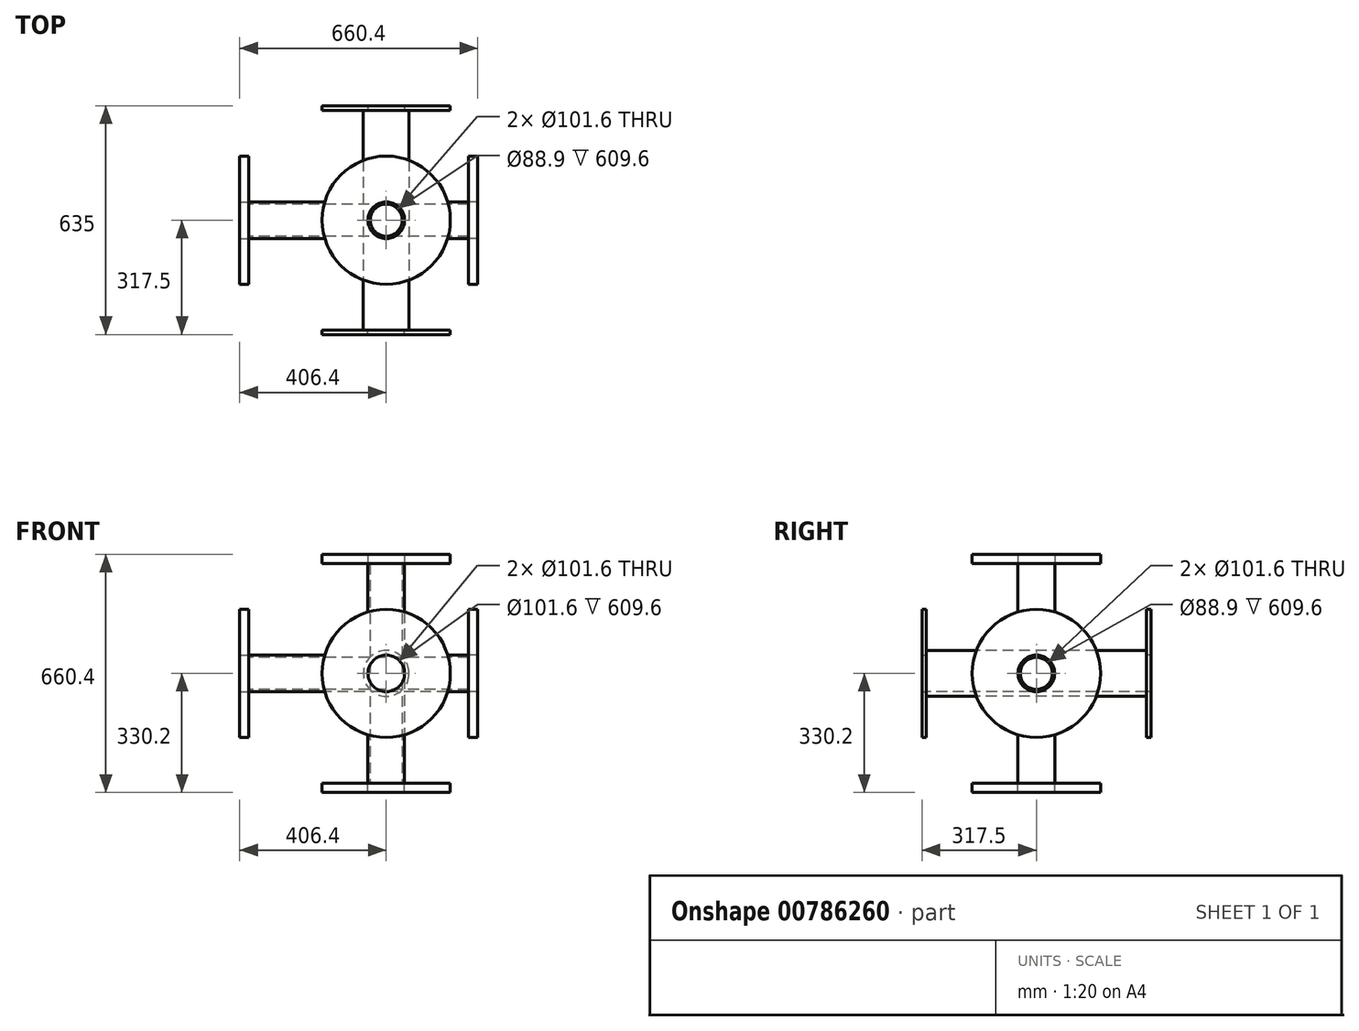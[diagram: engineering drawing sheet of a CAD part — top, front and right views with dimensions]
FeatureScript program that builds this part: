
annotation { "Feature Type Name" : "Feature", "Feature Type Description" : "" }
export const myFeature = defineFeature(function(context is Context, id is Id, definition is map)
    precondition{}
    {
        {
            var Q0;
            Q0=qCreatedBy(makeId("Top.planeOp"),FACE);
            var sketch = newSketch(context, id + "F0", { "sketchPlane" : qUnion([Q0])});
            skCircle(sketch, "E0", {"center": v(0, 0) * mm, "radius": 50.8 * mm});
            skCircle(sketch, "E1", {"center": v(0, 0) * mm, "radius": 44.45 * mm});
            skSolve(sketch);
        }
        {
            var Q0;
            Q0=makeQuery(id+"F0.imprint","IMPRINT",FACE,{"disambiguationData":[TD([[makeQuery(id+"F0.imprint","IMPRINT",EDGE,{"derivedFrom":sQuery(id+"F0.wireOp",EDGE,"E0")}),1.0]])]});
            extrude(context, id + "F1", {"entities" : qUnion([Q0]), "endBound" : BoundingType.SYMMETRIC, "depth" : 609.6 * mm, "offsetDistance" : 25.4 * mm});
        }
        {
            var Q0;
            Q0=makeQuery(id+"F1.opExtrude","CAP_FACE",FACE,{"disambiguationData":[OSD([sQuery(id+"F0.wireOp",EDGE,"E0"),sQuery(id+"F0.wireOp",EDGE,"E1")])],"isStart":false});
            var sketch = newSketch(context, id + "F2", { "sketchPlane" : qUnion([Q0])});
            skPoint(sketch, "E2", {"position": v(0, 0) * mm});
            skLineSegment(sketch, "E3", {"start": v(0, -50.8) * mm, "end": v(0, 50.8) * mm, "construction": true});
            skCircle(sketch, "E4", {"center": v(0, 0) * mm, "radius": 177.8 * mm});
            skCircle(sketch, "E5", {"center": v(0, 0) * mm, "radius": 50.8 * mm});
            skSolve(sketch);
        }
        {
            var Q0;
            Q0 = qSketchRegion(id + "F2", true);
            var Q1;
            Q1 = qSketchRegion(id + "F4", true);
            extrude(context, id + "F3", {"entities" : qUnion([Q0, Q1]), "depth" : 25.4 * mm, "offsetDistance" : 25.4 * mm});
        }
        {
            var Q0;
            Q0=makeQuery(id+"F1.opExtrude","CAP_FACE",FACE,{"disambiguationData":[OSD([sQuery(id+"F0.wireOp",EDGE,"E0"),sQuery(id+"F0.wireOp",EDGE,"E1")])],"isStart":true});
            var sketch = newSketch(context, id + "F4", { "sketchPlane" : qUnion([Q0])});
            skPoint(sketch, "E6", {"position": v(0, 0) * mm});
            skCircle(sketch, "E7", {"center": v(0, 0) * mm, "radius": 177.8 * mm});
            skSolve(sketch);
        }
        {
            var Q0;
            Q0=qCreatedBy(makeId("Right.planeOp"),FACE);
            var sketch = newSketch(context, id + "F5", { "sketchPlane" : qUnion([Q0])});
            skCircle(sketch, "E8", {"center": v(0, 0) * mm, "radius": 63.5 * mm});
            skCircle(sketch, "E9", {"center": v(0, 0) * mm, "radius": 50.8 * mm});
            skSolve(sketch);
        }
        {
            var Q0;
            Q0 = qSketchRegion(id + "F5", true);
            extrude(context, id + "F6", {"entities" : qUnion([Q0]), "endBound" : BoundingType.SYMMETRIC, "depth" : 609.6 * mm, "offsetDistance" : 25.4 * mm});
        }
        {
            var Q0;
            Q0=makeQuery(id+"F6.opExtrude","CAP_FACE",FACE,{"disambiguationData":[OSD([sQuery(id+"F5.wireOp",EDGE,"E8"),sQuery(id+"F5.wireOp",EDGE,"E9")])],"isStart":false});
            var sketch = newSketch(context, id + "F7", { "sketchPlane" : qUnion([Q0])});
            skPoint(sketch, "E10", {"position": v(0, 0) * mm});
            skCircle(sketch, "E11", {"center": v(0, 0) * mm, "radius": 177.8 * mm});
            skCircle(sketch, "E12", {"center": v(0, 0) * mm, "radius": 50.8 * mm});
            skSolve(sketch);
        }
        {
            var Q0;
            Q0 = qSketchRegion(id + "F7", true);
            extrude(context, id + "F8", {"entities" : qUnion([Q0]), "depth" : 12.7 * mm, "offsetDistance" : 25.4 * mm});
        }
        {
            var Q0;
            Q0=makeQuery(id+"F8.opExtrude","SWEPT_BODY",BODY,{"disambiguationData":[OSD([sQuery(id+"F7.wireOp",EDGE,"E11"),sQuery(id+"F7.wireOp",EDGE,"E12")])]});
            var Q1;
            Q1=qCreatedBy(makeId("Right.planeOp"),FACE);
            mirror(context, id + "F9", {"entities" : qUnion([Q0]), "mirrorPlane" : qUnion([Q1])});
        }
        {
            var Q0;
            Q0=makeQuery(id+"Fdzxom4iDK7pz1L_1.opExtrude","SWEPT_BODY",BODY,{"disambiguationData":[OSD([sQuery(id+"F4.wireOp",EDGE,"E7")])]});
            var Q1;
            Q1=makeQuery(id+"F1.opExtrude","SWEPT_BODY",BODY,{"disambiguationData":[OSD([sQuery(id+"F0.wireOp",EDGE,"E0"),sQuery(id+"F0.wireOp",EDGE,"E1")])]});
            var Q2;
            Q2=makeQuery(id+"F3.opExtrude","SWEPT_BODY",BODY,{"disambiguationData":[OSD([sQuery(id+"F2.wireOp",EDGE,"E4")])]});
            var Q3;
            Q3=makeQuery(id+"F9.opPattern","COPY",EDGE,{"derivedFrom":makeQuery(id+"F8.opExtrude","CAP_EDGE",EDGE,{"disambiguationData":[OSD([sQuery(id+"F7.wireOp",EDGE,"E11")])],"isStart":false}),"instanceName":"1"});
            transform(context, id + "F10", {"entities" : qUnion([Q0, Q1, Q2]), "transformType" : TransformType.ROTATION, "transformAxis" : qUnion([Q3]), "angle" : 90 * degree, "makeCopy" : false});
        }
        {
            var Q0;
            Q0=makeQuery(id+"Fdzxom4iDK7pz1L_1.opExtrude","SWEPT_BODY",BODY,{"disambiguationData":[OSD([sQuery(id+"F4.wireOp",EDGE,"E7")])]});
            var Q1;
            Q1=makeQuery(id+"F1.opExtrude","SWEPT_BODY",BODY,{"disambiguationData":[OSD([sQuery(id+"F0.wireOp",EDGE,"E0"),sQuery(id+"F0.wireOp",EDGE,"E1")])]});
            var Q2;
            Q2=makeQuery(id+"F3.opExtrude","SWEPT_BODY",BODY,{"disambiguationData":[OSD([sQuery(id+"F2.wireOp",EDGE,"E4")])]});
            var Q3;
            Q3=makeQuery(id+"F6.opExtrude","SWEPT_FACE",FACE,{"disambiguationData":[OSD([sQuery(id+"F5.wireOp",EDGE,"E8")])]});
            transform(context, id + "F11", {"entities" : qUnion([Q0, Q1, Q2]), "transformType" : TransformType.ROTATION, "transformAxis" : qUnion([Q3]), "angle" : 90 * degree, "makeCopy" : false});
        }
        {
            var Q0;
            Q0=makeQuery(id+"F3.opExtrude","SWEPT_BODY",BODY,{"disambiguationData":[OSD([sQuery(id+"F2.wireOp",EDGE,"E4"),sQuery(id+"F2.wireOp",EDGE,"E5")])]});
            var Q1;
            Q1=qCreatedBy(makeId("Top.planeOp"),FACE);
            mirror(context, id + "F12", {"entities" : qUnion([Q0]), "mirrorPlane" : qUnion([Q1])});
        }
        {
            var Q0;
            Q0=makeQuery(id+"F6.opExtrude","SWEPT_BODY",BODY,{"disambiguationData":[OSD([sQuery(id+"F5.wireOp",EDGE,"E8"),sQuery(id+"F5.wireOp",EDGE,"E9")])]});
            var Q1;
            Q1=makeQuery(id+"F9.opPattern","COPY",BODY,{"derivedFrom":makeQuery(id+"F8.opExtrude","SWEPT_BODY",BODY,{"disambiguationData":[OSD([sQuery(id+"F7.wireOp",EDGE,"E11"),sQuery(id+"F7.wireOp",EDGE,"E12")])]}),"instanceName":"1"});
            var Q2;
            Q2=makeQuery(id+"F8.opExtrude","SWEPT_BODY",BODY,{"disambiguationData":[OSD([sQuery(id+"F7.wireOp",EDGE,"E11"),sQuery(id+"F7.wireOp",EDGE,"E12")])]});
            var Q3;
            Q3=makeQuery(id+"F3.opExtrude","CAP_EDGE",EDGE,{"disambiguationData":[OSD([sQuery(id+"F2.wireOp",EDGE,"E4")])],"isStart":false});
            transform(context, id + "F13", {"entities" : qUnion([Q0, Q1, Q2]), "transformType" : TransformType.ROTATION, "transformAxis" : qUnion([Q3]), "angle" : 90 * degree, "makeCopy" : false});
        }
        {
            var Q0;
            Q0=makeQuery(id+"F1.opExtrude","SWEPT_BODY",BODY,{"disambiguationData":[OSD([sQuery(id+"F0.wireOp",EDGE,"E0"),sQuery(id+"F0.wireOp",EDGE,"E1")])]});
            var Q1;
            Q1=makeQuery(id+"F3.opExtrude","SWEPT_BODY",BODY,{"disambiguationData":[OSD([sQuery(id+"F2.wireOp",EDGE,"E4"),sQuery(id+"F2.wireOp",EDGE,"E5")])]});
            var Q2;
            Q2=makeQuery(id+"F12.opPattern","COPY",BODY,{"derivedFrom":makeQuery(id+"F3.opExtrude","SWEPT_BODY",BODY,{"disambiguationData":[OSD([sQuery(id+"F2.wireOp",EDGE,"E4"),sQuery(id+"F2.wireOp",EDGE,"E5")])]}),"instanceName":"1"});
            var Q3;
            Q3=makeQuery(id+"F8.opExtrude","CAP_EDGE",EDGE,{"disambiguationData":[OSD([sQuery(id+"F7.wireOp",EDGE,"E11")])],"isStart":false});
            transform(context, id + "F14", {"entities" : qUnion([Q0, Q1, Q2]), "transformType" : TransformType.ROTATION, "transformAxis" : qUnion([Q3]), "angle" : 90 * degree, "makeCopy" : true});
        }
        {
            var Q0;
            Q0=makeQuery(id+"F14.opPattern","COPY",BODY,{"derivedFrom":makeQuery(id+"F1.opExtrude","SWEPT_BODY",BODY,{"disambiguationData":[OSD([sQuery(id+"F0.wireOp",EDGE,"E0"),sQuery(id+"F0.wireOp",EDGE,"E1")])]}),"instanceName":"1"});
            var Q1;
            Q1=makeQuery(id+"F14.opPattern","COPY",BODY,{"derivedFrom":makeQuery(id+"F12.opPattern","COPY",BODY,{"derivedFrom":makeQuery(id+"F3.opExtrude","SWEPT_BODY",BODY,{"disambiguationData":[OSD([sQuery(id+"F2.wireOp",EDGE,"E4"),sQuery(id+"F2.wireOp",EDGE,"E5")])]}),"instanceName":"1"}),"instanceName":"1"});
            var Q2;
            Q2=makeQuery(id+"F14.opPattern","COPY",BODY,{"derivedFrom":makeQuery(id+"F3.opExtrude","SWEPT_BODY",BODY,{"disambiguationData":[OSD([sQuery(id+"F2.wireOp",EDGE,"E4"),sQuery(id+"F2.wireOp",EDGE,"E5")])]}),"instanceName":"1"});
            transform(context, id + "F15", {"entities" : qUnion([Q0, Q1, Q2]), "transformType" : TransformType.TRANSLATION_3D, "dx" : -50.8 * mm, "dy" : 0 * mm, "dz" : 0 * mm, "makeCopy" : false});
        }
        {
            var Q0;
            Q0=makeQuery(id+"F14.opPattern","COPY",BODY,{"derivedFrom":makeQuery(id+"F1.opExtrude","SWEPT_BODY",BODY,{"disambiguationData":[OSD([sQuery(id+"F0.wireOp",EDGE,"E0"),sQuery(id+"F0.wireOp",EDGE,"E1")])]}),"instanceName":"1"});
            var Q1;
            Q1=makeQuery(id+"F14.opPattern","COPY",BODY,{"derivedFrom":makeQuery(id+"F12.opPattern","COPY",BODY,{"derivedFrom":makeQuery(id+"F3.opExtrude","SWEPT_BODY",BODY,{"disambiguationData":[OSD([sQuery(id+"F2.wireOp",EDGE,"E4"),sQuery(id+"F2.wireOp",EDGE,"E5")])]}),"instanceName":"1"}),"instanceName":"1"});
            var Q2;
            Q2=makeQuery(id+"F14.opPattern","COPY",BODY,{"derivedFrom":makeQuery(id+"F3.opExtrude","SWEPT_BODY",BODY,{"disambiguationData":[OSD([sQuery(id+"F2.wireOp",EDGE,"E4"),sQuery(id+"F2.wireOp",EDGE,"E5")])]}),"instanceName":"1"});
            transform(context, id + "F16", {"entities" : qUnion([Q0, Q1, Q2]), "transformType" : TransformType.TRANSLATION_3D, "dx" : -25.4 * mm, "dy" : 0 * mm, "dz" : 0 * mm, "makeCopy" : false});
        }
    });
